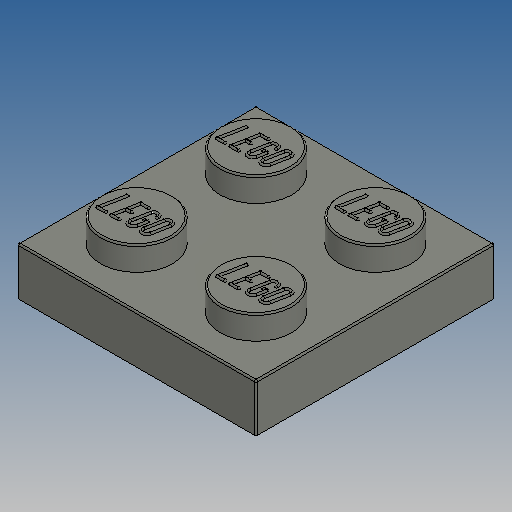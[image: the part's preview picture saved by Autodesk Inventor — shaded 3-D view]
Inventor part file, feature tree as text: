
AUTODESK INVENTOR PART (.ipt)
format: ipt  version: 2025 (Build 290162010, 162A)  size: 1,532,928 bytes
history: native  units: in
note: dims shown in document units (in); Inventor stores cm internally (conversion verified against a paired STEP export)
features: extrude x4, sketch x4, fillet x2, pattern_linear x2, other x1
ambient origin geometry x8: Origin, YZ Plane, XZ Plane, XY Plane, X Axis, Y Axis, Z Axis, Center Point
bodies: Solid1 (feature_tree)
feature tree (13):
  extrude  "Extrusion1"  Depth=0.6299in
  extrude  "Extrusion4"  Depth=0.063in
  other  "LEGO:1"
  fillet  "Fillet2"  Radius=0.063in
  pattern_linear  "Rectangular Pattern1"  Spacing1=0.189in  [1 undecoded]
  sketch  "Sketch3"  dims[d4=0.126in d5=0.0in d7=0.0591in d8=0.063in d11=0.063in d12=0.0in]
  extrude  "Extrusion2"  Depth=0.063in
  extrude  "Extrusion5"  Depth=0.189in
  pattern_linear  "Rectangular Pattern2"  Spacing1=0.1575in  [1 undecoded]
  fillet  "Fillet1"  Radius=0.1575in
  sketch  "Sketch2"  dims[d0=0.6299in d1=0.6299in]
  sketch  "Sketch9"  dims[d22=0.0039in]
  sketch  "Sketch10"  dims[d60=0.2564in d61=0.189in d62=0.063in d63=0.189in d64=0.1575in d65=0.1575in d66=0.063in d67=0.0in d68=0.0039in d69=0.7874in d71=0.315in d72=0.7874in d74=0.315in d75=0.315in d76=0.315in d77=0.0709in d78=0.0in d79=0.3937in d81=0.315in d82=0.3937in d84=0.315in d85=0.0in d86=0.0in d87=0.0in d88=0.0in d89=0.0in d90=0.0in d91=0.0in d92=0.0079in d93=0.0732in d94=0.0281in d95=0.035in d96=0.0079in d97=0.0139in d98=0.0281in d99=0.035in d100=0.0281in d101=0.0159in d102=0.0177in d103=0.035in d104=0.5428in]
note: 2 required parameter values undecoded (feature->parameter linkage not recoverable at this tier; creation-order binding heuristic only, values carry confidence <= 0.55)
